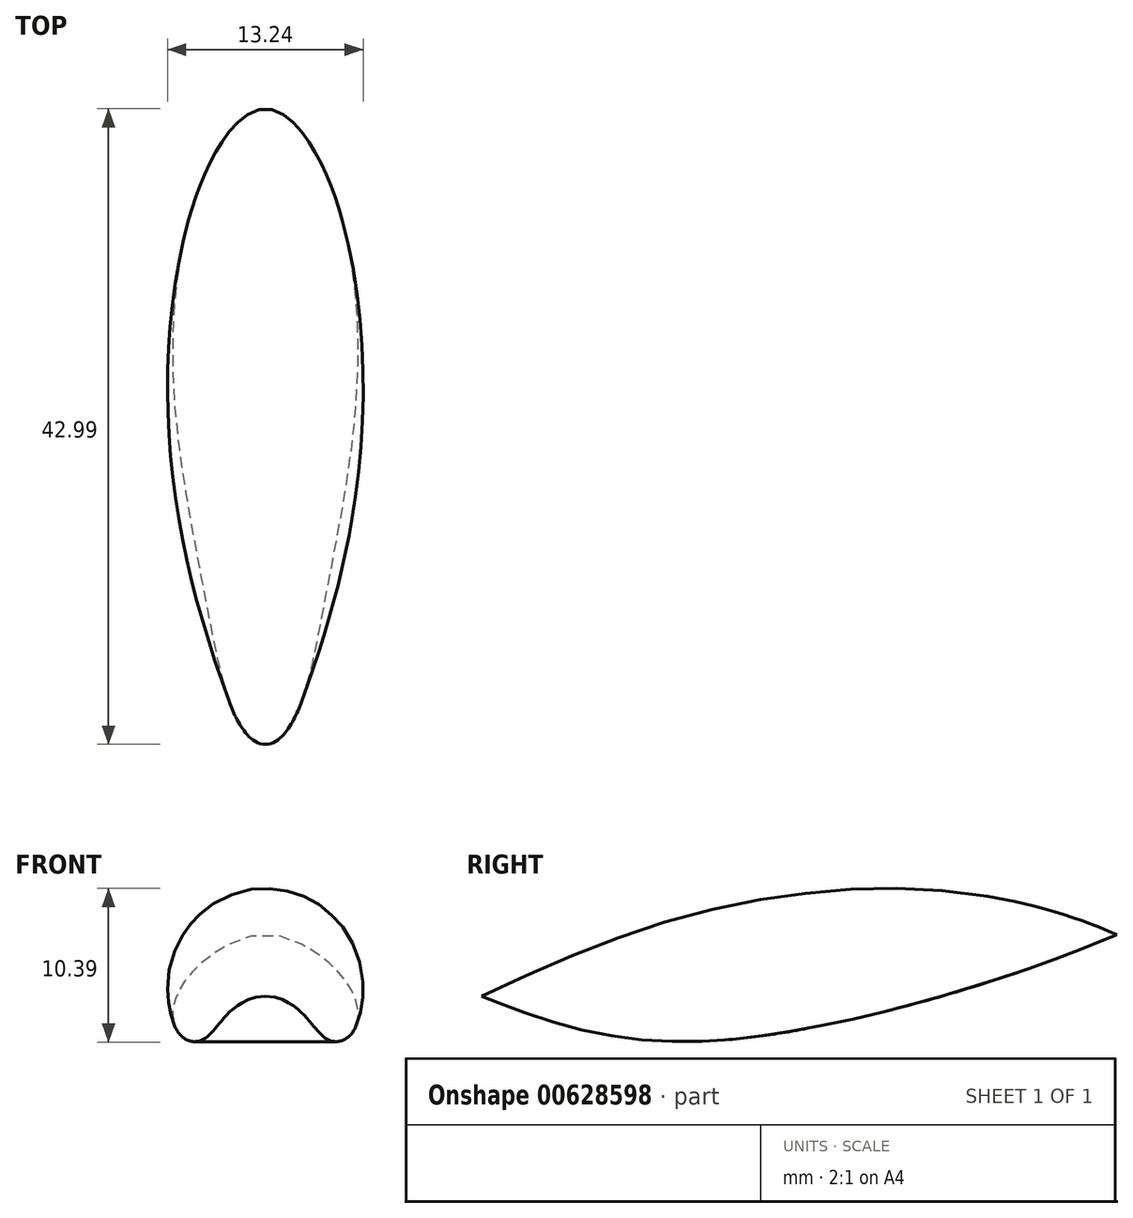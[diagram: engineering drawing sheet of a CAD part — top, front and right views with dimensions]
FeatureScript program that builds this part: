
annotation { "Feature Type Name" : "Feature", "Feature Type Description" : "" }
export const myFeature = defineFeature(function(context is Context, id is Id, definition is map)
    precondition{}
    {
        {
            var Q0;
            Q0=qCreatedBy(makeId("Right.planeOp"),FACE);
            var sketch = newSketch(context, id + "F0", { "sketchPlane" : qUnion([Q0])});
            skLineSegment(sketch, "E0", {"start": v(-61.43, 0) * mm, "end": v(63.71, 0) * mm});
            skLineSegment(sketch, "E1", {"start": v(63.71, 0) * mm, "end": v(63.71, 21.98) * mm});
            skCircle(sketch, "E2", {"center": v(-32.12, 0) * mm, "radius": 12 * mm});
            skCircle(sketch, "E3", {"center": v(39.07, 2) * mm, "radius": 12 * mm});
            skFitSpline(sketch, "E4", {"points": [v(-61.43, 0) * mm, v(-34.2, 19.3) * mm, v(-22.85, 20.07) * mm, v(-9.5, 15.15) * mm, v(4.65, 13.09) * mm, v(29.55, 19.53) * mm, v(44.48, 23.8) * mm, v(63.71, 21.98) * mm], "startDerivative": vector(151.63, 145.86) * mm, "endDerivative": vector(14.11, 0) * mm});
            skSolve(sketch);
        }
        {
            var Q0;
            Q0=qCreatedBy(makeId("Top.planeOp"),FACE);
            cPlane(context, id + "F1", {"entities" : qUnion([Q0]), "cplaneType" : CPlaneType.OFFSET, "offset" : 3 * mm, "width" : 150 * mm, "height" : 150 * mm});
        }
        {
            var Q0;
            {var subQ0=sQuery(id+"F0.wireOp",EDGE,"E1");Q0=makeQuery(id+"F0.imprint","IMPRINT",FACE,{"disambiguationData":[TD([[makeQuery(id+"F0.imprint","IMPRINT",EDGE,{"derivedFrom":subQ0}),1.0]])]});}
            var Q1;
            {var subQ0=sQuery(id+"F0.wireOp",EDGE,"E2");var subQ1=sQuery(id+"F0.wireOp",EDGE,"E0");var subQ2=makeQuery(id+"F0.imprint","INTERSECT",VERTEX,{"disambiguationData":[OD(0.0)],"derivedFrom":[subQ1,subQ0]});Q1=makeQuery(id+"F0.imprint","IMPRINT",FACE,{"disambiguationData":[TD([[makeQuery(id+"F0.imprint","IMPRINT",EDGE,{"disambiguationData":[TD([[subQ2,-1.0]])],"derivedFrom":subQ1}),1.0]])]});}
            var Q2;
            {var subQ0=sQuery(id+"F0.wireOp",EDGE,"E3");var subQ1=sQuery(id+"F0.wireOp",EDGE,"E0");var subQ2=makeQuery(id+"F0.imprint","INTERSECT",VERTEX,{"disambiguationData":[OD(0.0)],"derivedFrom":[subQ1,subQ0]});Q2=makeQuery(id+"F0.imprint","IMPRINT",FACE,{"disambiguationData":[TD([[makeQuery(id+"F0.imprint","IMPRINT",EDGE,{"disambiguationData":[TD([[subQ2,-1.0]])],"derivedFrom":subQ1}),1.0]])]});}
            extrude(context, id + "F2", {"entities" : qUnion([Q0, Q1, Q2]), "endBound" : BoundingType.SYMMETRIC, "depth" : 60 * mm});
        }
        {
            var Q0;
            Q0=qCreatedBy(makeId("Right.planeOp"),FACE);
            var sketch = newSketch(context, id + "F3", { "sketchPlane" : qUnion([Q0])});
            skFitSpline(sketch, "E5", {"points": [v(-15.28, 14.34) * mm, v(2.7, 21.63) * mm, v(24.38, 22.44) * mm, v(33.93, 18.55) * mm, v(33.93, 18.23) * mm], "startDerivative": vector(49.99, 24.46) * mm, "endDerivative": vector(-2.74, -6.39) * mm});
            skLineSegment(sketch, "E6", {"start": v(-15.28, 14.34) * mm, "end": v(33.97, 18.32) * mm});
            skSolve(sketch);
        }
        {
            var Q0;
            {var subQ0=sQuery(id+"F3.wireOp",EDGE,"E6");var subQ1=sQuery(id+"F3.wireOp",EDGE,"E5");var subQ2=makeQuery(id+"F3.imprint","INTERSECT",VERTEX,{"disambiguationData":[OD(0.0)],"derivedFrom":[subQ1,subQ0]});Q0=makeQuery(id+"F3.imprint","IMPRINT",FACE,{"disambiguationData":[TD([[makeQuery(id+"F3.imprint","IMPRINT",EDGE,{"disambiguationData":[TD([[subQ2,-1.0]])],"derivedFrom":subQ1}),-1.0]])]});}
            var Q1;
            Q1=qConstructionFilter(qBodyType(qCreatedBy(id+"F3",EDGE),BodyType.WIRE),ConstructionObject.NO);
            var Q2;
            Q2=sQuery(id+"F3.wireOp",EDGE,"E6");
            revolve(context, id + "F4", {"operationType" : NewBodyOperationType.ADD, "entities" : qUnion([Q0]), "surfaceEntities" : qUnion([Q1]), "axis" : qUnion([Q2]), "revolveType" : RevolveType.SYMMETRIC, "angle" : 360 * degree});
        }
        {
            var Q0;
            Q0=qCreatedBy(makeId("Right.planeOp"),FACE);
            var sketch = newSketch(context, id + "F5", { "sketchPlane" : qUnion([Q0])});
            skLineSegment(sketch, "E7", {"start": v(-14.66, 16.96) * mm, "end": v(-23.22, 27.93) * mm});
            skLineSegment(sketch, "E8", {"start": v(-23.22, 27.93) * mm, "end": v(-61.74, 13.85) * mm});
            skLineSegment(sketch, "E9", {"start": v(-61.74, 13.85) * mm, "end": v(-57.48, 2.18) * mm});
            skFitSpline(sketch, "E10", {"points": [v(-57.48, 2.18) * mm, v(-36.9, 15.8) * mm, v(-25.53, 18.11) * mm, v(-14.66, 16.96) * mm], "startDerivative": vector(36.14, 27.84) * mm, "endDerivative": vector(35.2, -5.65) * mm});
            skLineSegment(sketch, "E11", {"start": v(34.04, 20.87) * mm, "end": v(39.38, 26.78) * mm});
            skLineSegment(sketch, "E12", {"start": v(39.38, 26.78) * mm, "end": v(68, 24.85) * mm});
            skLineSegment(sketch, "E13", {"start": v(68, 24.85) * mm, "end": v(63.22, 11.9) * mm});
            skFitSpline(sketch, "E14", {"points": [v(34.04, 20.87) * mm, v(45.25, 21.94) * mm, v(58.77, 18.94) * mm, v(63.22, 11.9) * mm], "startDerivative": vector(31.03, 4.85) * mm, "endDerivative": vector(10.27, -27.45) * mm});
            skSolve(sketch);
        }
        {
            var Q0;
            Q0=makeQuery(id+"F5.imprint","IMPRINT",FACE,{"disambiguationData":[TD([[makeQuery(id+"F5.imprint","IMPRINT",EDGE,{"derivedFrom":sQuery(id+"F5.wireOp",EDGE,"E7")}),1.0]])]});
            var Q1;
            Q1=makeQuery(id+"F5.imprint","IMPRINT",FACE,{"disambiguationData":[TD([[makeQuery(id+"F5.imprint","IMPRINT",EDGE,{"derivedFrom":sQuery(id+"F5.wireOp",EDGE,"E11")}),-1.0]])]});
            extrude(context, id + "F6", {"entities" : qUnion([Q0, Q1]), "operationType" : NewBodyOperationType.REMOVE, "endBound" : BoundingType.SYMMETRIC, "oppositeDirection" : true, "depth" : 35 * mm});
        }
        {
            var Q0;
            Q0=makeQuery(id+"F6.boolean.opBoolean","INTERSECT",EDGE,{"derivedFrom":[makeQuery(id+"F2.opExtrude","SWEPT_FACE",FACE,{"disambiguationData":[OSD([sQuery(id+"F0.wireOp",EDGE,"E4")])]}),makeQuery(id+"F6.opExtrude","CAP_FACE",FACE,{"disambiguationData":[OSD([sQuery(id+"F5.wireOp",EDGE,"E7"),sQuery(id+"F5.wireOp",EDGE,"E8"),sQuery(id+"F5.wireOp",EDGE,"E9"),sQuery(id+"F5.wireOp",EDGE,"E10")])],"isStart":false})]});
            var Q1;
            Q1=makeQuery(id+"F6.boolean.opBoolean","INTERSECT",EDGE,{"derivedFrom":[makeQuery(id+"F2.opExtrude","SWEPT_FACE",FACE,{"disambiguationData":[OSD([sQuery(id+"F0.wireOp",EDGE,"E4")])]}),makeQuery(id+"F6.opExtrude","CAP_FACE",FACE,{"disambiguationData":[OSD([sQuery(id+"F5.wireOp",EDGE,"E7"),sQuery(id+"F5.wireOp",EDGE,"E8"),sQuery(id+"F5.wireOp",EDGE,"E9"),sQuery(id+"F5.wireOp",EDGE,"E10")])],"isStart":true})]});
            var Q2;
            Q2=makeQuery(id+"F6.boolean.opBoolean","INTERSECT",EDGE,{"derivedFrom":[makeQuery(id+"F2.opExtrude","SWEPT_FACE",FACE,{"disambiguationData":[OSD([sQuery(id+"F0.wireOp",EDGE,"E4")])]}),makeQuery(id+"F6.opExtrude","SWEPT_FACE",FACE,{"disambiguationData":[OSD([sQuery(id+"F5.wireOp",EDGE,"E9")])]})]});
            var Q3;
            Q3=makeQuery(id+"F6.boolean.opBoolean","INTERSECT",EDGE,{"disambiguationData":[OD(0.0)],"derivedFrom":[makeQuery(id+"F2.opExtrude","SWEPT_FACE",FACE,{"disambiguationData":[OSD([sQuery(id+"F0.wireOp",EDGE,"E4")])]}),makeQuery(id+"F6.opExtrude","SWEPT_FACE",FACE,{"disambiguationData":[OSD([sQuery(id+"F5.wireOp",EDGE,"E7")])]})]});
            var Q4;
            Q4=makeQuery(id+"F6.boolean.opBoolean","INTERSECT",EDGE,{"disambiguationData":[OD(1.0)],"derivedFrom":[makeQuery(id+"F2.opExtrude","SWEPT_FACE",FACE,{"disambiguationData":[OSD([sQuery(id+"F0.wireOp",EDGE,"E4")])]}),makeQuery(id+"F6.opExtrude","SWEPT_FACE",FACE,{"disambiguationData":[OSD([sQuery(id+"F5.wireOp",EDGE,"E7")])]})]});
            var Q5;
            Q5=makeQuery(id+"F2.opExtrude","CAP_EDGE",EDGE,{"disambiguationData":[OSD([sQuery(id+"F0.wireOp",EDGE,"E4")])],"isStart":true});
            var Q6;
            Q6=makeQuery(id+"F2.opExtrude","CAP_EDGE",EDGE,{"disambiguationData":[OSD([sQuery(id+"F0.wireOp",EDGE,"E4")])],"isStart":false});
            var Q7;
            Q7=makeQuery(id+"F6.boolean.opBoolean","INTERSECT",EDGE,{"derivedFrom":[makeQuery(id+"F2.opExtrude","SWEPT_FACE",FACE,{"disambiguationData":[OSD([sQuery(id+"F0.wireOp",EDGE,"E4")])]}),makeQuery(id+"F6.opExtrude","CAP_FACE",FACE,{"disambiguationData":[OSD([sQuery(id+"F5.wireOp",EDGE,"E11"),sQuery(id+"F5.wireOp",EDGE,"E12"),sQuery(id+"F5.wireOp",EDGE,"E13"),sQuery(id+"F5.wireOp",EDGE,"E14")])],"isStart":false})]});
            var Q8;
            Q8=makeQuery(id+"F6.boolean.opBoolean","INTERSECT",EDGE,{"derivedFrom":[makeQuery(id+"F2.opExtrude","SWEPT_FACE",FACE,{"disambiguationData":[OSD([sQuery(id+"F0.wireOp",EDGE,"E4")])]}),makeQuery(id+"F6.opExtrude","SWEPT_FACE",FACE,{"disambiguationData":[OSD([sQuery(id+"F5.wireOp",EDGE,"E11")])]})]});
            var Q9;
            Q9=makeQuery(id+"F6.boolean.opBoolean","INTERSECT",EDGE,{"derivedFrom":[makeQuery(id+"F2.opExtrude","SWEPT_FACE",FACE,{"disambiguationData":[OSD([sQuery(id+"F0.wireOp",EDGE,"E4")])]}),makeQuery(id+"F6.opExtrude","CAP_FACE",FACE,{"disambiguationData":[OSD([sQuery(id+"F5.wireOp",EDGE,"E11"),sQuery(id+"F5.wireOp",EDGE,"E12"),sQuery(id+"F5.wireOp",EDGE,"E13"),sQuery(id+"F5.wireOp",EDGE,"E14")])],"isStart":true})]});
            var Q10;
            Q10=makeQuery(id+"F6.boolean.opBoolean","INTERSECT",EDGE,{"derivedFrom":[makeQuery(id+"F2.opExtrude","SWEPT_FACE",FACE,{"disambiguationData":[OSD([sQuery(id+"F0.wireOp",EDGE,"E1")])]}),makeQuery(id+"F6.opExtrude","CAP_FACE",FACE,{"disambiguationData":[OSD([sQuery(id+"F5.wireOp",EDGE,"E11"),sQuery(id+"F5.wireOp",EDGE,"E12"),sQuery(id+"F5.wireOp",EDGE,"E13"),sQuery(id+"F5.wireOp",EDGE,"E14")])],"isStart":true})]});
            var Q11;
            Q11=makeQuery(id+"F6.boolean.opBoolean","INTERSECT",EDGE,{"derivedFrom":[makeQuery(id+"F2.opExtrude","SWEPT_FACE",FACE,{"disambiguationData":[OSD([sQuery(id+"F0.wireOp",EDGE,"E1")])]}),makeQuery(id+"F6.opExtrude","SWEPT_FACE",FACE,{"disambiguationData":[OSD([sQuery(id+"F5.wireOp",EDGE,"E14")])]})]});
            var Q12;
            Q12=makeQuery(id+"F6.boolean.opBoolean","INTERSECT",EDGE,{"derivedFrom":[makeQuery(id+"F2.opExtrude","SWEPT_FACE",FACE,{"disambiguationData":[OSD([sQuery(id+"F0.wireOp",EDGE,"E1")])]}),makeQuery(id+"F6.opExtrude","CAP_FACE",FACE,{"disambiguationData":[OSD([sQuery(id+"F5.wireOp",EDGE,"E11"),sQuery(id+"F5.wireOp",EDGE,"E12"),sQuery(id+"F5.wireOp",EDGE,"E13"),sQuery(id+"F5.wireOp",EDGE,"E14")])],"isStart":false})]});
            var Q13;
            {var subQ0=sQuery(id+"F0.wireOp",EDGE,"E4");var subQ1=sQuery(id+"F0.wireOp",EDGE,"E1");Q13=makeQuery(id+"F6.boolean.opBoolean","SPLIT",EDGE,{"disambiguationData":[TD([makeQuery(id+"F2.opExtrude","CAP_FACE",FACE,{"disambiguationData":[OSD([sQuery(id+"F0.wireOp",EDGE,"E0"),subQ1,subQ0])],"isStart":true})])],"derivedFrom":makeQuery(id+"F2.opExtrude","SWEPT_EDGE",EDGE,{"disambiguationData":[OSD([subQ1,subQ0])]})});}
            var Q14;
            Q14=makeQuery(id+"F2.opExtrude","CAP_EDGE",EDGE,{"disambiguationData":[OSD([sQuery(id+"F0.wireOp",EDGE,"E1")])],"isStart":true});
            var Q15;
            Q15=makeQuery(id+"F2.opExtrude","CAP_EDGE",EDGE,{"disambiguationData":[OSD([sQuery(id+"F0.wireOp",EDGE,"E1")])],"isStart":false});
            fillet(context, id + "F7", {"entities" : qUnion([Q0, Q1, Q2, Q3, Q4, Q5, Q6, Q7, Q8, Q9, Q10, Q11, Q12, Q13, Q14, Q15]), "radius" : 1 * mm, "tangentPropagation" : true, "allowEdgeOverflow" : false});
        }
        {
            var Q0;
            {var subQ0=sQuery(id+"F0.wireOp",EDGE,"E2");var subQ1=sQuery(id+"F0.wireOp",EDGE,"E0");var subQ2=makeQuery(id+"F0.imprint","INTERSECT",VERTEX,{"disambiguationData":[OD(0.0)],"derivedFrom":[subQ1,subQ0]});Q0=makeQuery(id+"F0.imprint","IMPRINT",FACE,{"disambiguationData":[TD([[makeQuery(id+"F0.imprint","IMPRINT",EDGE,{"disambiguationData":[TD([[subQ2,-1.0]])],"derivedFrom":subQ1}),1.0]])]});}
            var Q1;
            {var subQ0=sQuery(id+"F0.wireOp",EDGE,"E3");var subQ1=sQuery(id+"F0.wireOp",EDGE,"E0");var subQ2=makeQuery(id+"F0.imprint","INTERSECT",VERTEX,{"disambiguationData":[OD(0.0)],"derivedFrom":[subQ1,subQ0]});Q1=makeQuery(id+"F0.imprint","IMPRINT",FACE,{"disambiguationData":[TD([[makeQuery(id+"F0.imprint","IMPRINT",EDGE,{"disambiguationData":[TD([[subQ2,-1.0]])],"derivedFrom":subQ1}),1.0]])]});}
            extrude(context, id + "F8", {"entities" : qUnion([Q0, Q1]), "operationType" : NewBodyOperationType.REMOVE, "endBound" : BoundingType.SYMMETRIC, "oppositeDirection" : true, "depth" : 60 * mm});
        }
    });
